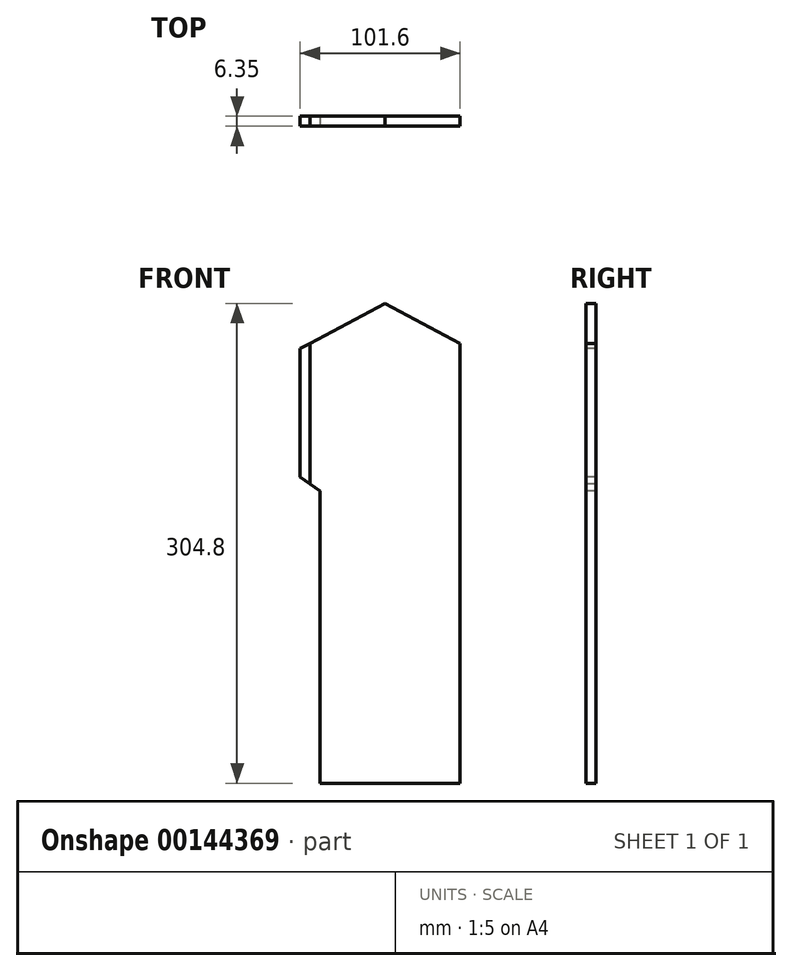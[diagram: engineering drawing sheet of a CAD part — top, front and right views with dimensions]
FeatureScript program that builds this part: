
annotation { "Feature Type Name" : "Feature", "Feature Type Description" : "" }
export const myFeature = defineFeature(function(context is Context, id is Id, definition is map)
    precondition{}
    {
        {
            var Q0;
            Q0=qCreatedBy(makeId("Front.planeOp"),FACE);
            var sketch = newSketch(context, id + "F0", { "sketchPlane" : qUnion([Q0])});
            skLineSegment(sketch, "E0.bottom", {"start": v(0, 0) * mm, "end": v(95.25, 0) * mm});
            skLineSegment(sketch, "E0.top", {"start": v(0, 279.4) * mm, "end": v(95.25, 279.4) * mm});
            skLineSegment(sketch, "E0.left", {"start": v(0, 0) * mm, "end": v(0, 279.4) * mm});
            skLineSegment(sketch, "E0.right", {"start": v(95.25, 0) * mm, "end": v(95.25, 279.4) * mm});
            skLineSegment(sketch, "E1", {"start": v(0, 279.4) * mm, "end": v(47.62, 304.8) * mm});
            skLineSegment(sketch, "E2", {"start": v(47.62, 304.8) * mm, "end": v(95.25, 279.4) * mm});
            skLineSegment(sketch, "E3", {"start": v(47.62, 304.8) * mm, "end": v(47.62, 279.4) * mm, "construction": true});
            skSolve(sketch);
        }
        {
            var Q0;
            Q0 = qSketchRegion(id + "F0", true);
            extrude(context, id + "F1", {"entities" : qUnion([Q0]), "depth" : 6.35 * mm});
        }
        {
            var Q0;
            Q0=makeQuery(id+"F1.opExtrude","CAP_FACE",FACE,{"disambiguationData":[OSD([sQuery(id+"F0.wireOp",EDGE,"E0.bottom"),sQuery(id+"F0.wireOp",EDGE,"E0.top"),sQuery(id+"F0.wireOp",EDGE,"E0.left"),sQuery(id+"F0.wireOp",EDGE,"E0.right")])],"isStart":false});
            var sketch = newSketch(context, id + "F2", { "sketchPlane" : qUnion([Q0])});
            skLineSegment(sketch, "E4", {"start": v(6.35, 0) * mm, "end": v(6.35, 177.8) * mm});
            skLineSegment(sketch, "E5", {"start": v(6.35, 177.8) * mm, "end": v(0, 182.28) * mm});
            skLineSegment(sketch, "E6", {"start": v(6.35, 0) * mm, "end": v(0, 0) * mm});
            skLineSegment(sketch, "E7", {"start": v(0, 0) * mm, "end": v(0, 182.28) * mm});
            skSolve(sketch);
        }
        {
            var Q0;
            Q0 = qSketchRegion(id + "F2", true);
            extrude(context, id + "F3", {"entities" : qUnion([Q0]), "operationType" : NewBodyOperationType.REMOVE, "oppositeDirection" : true, "depth" : 25.4 * mm});
        }
        {
            var Q0;
            Q0=makeQuery(id+"F1.opExtrude","CAP_FACE",FACE,{"disambiguationData":[OSD([sQuery(id+"F0.wireOp",EDGE,"E0.bottom"),sQuery(id+"F0.wireOp",EDGE,"E0.top"),sQuery(id+"F0.wireOp",EDGE,"E0.left"),sQuery(id+"F0.wireOp",EDGE,"E0.right")])],"isStart":false});
            var sketch = newSketch(context, id + "F4", { "sketchPlane" : qUnion([Q0])});
            skLineSegment(sketch, "E8", {"start": v(6.35, 177.8) * mm, "end": v(6.35, 185.57) * mm});
            skLineSegment(sketch, "E9", {"start": v(6.35, 185.57) * mm, "end": v(0, 190.06) * mm});
            skLineSegment(sketch, "E10", {"start": v(0, 190.06) * mm, "end": v(0, 182.28) * mm});
            skLineSegment(sketch, "E11", {"start": v(0, 182.28) * mm, "end": v(6.35, 177.8) * mm});
            skSolve(sketch);
        }
        {
            var Q0;
            Q0 = qSketchRegion(id + "F4", true);
            extrude(context, id + "F5", {"entities" : qUnion([Q0]), "operationType" : NewBodyOperationType.REMOVE, "oppositeDirection" : true, "depth" : 6.35 * mm});
        }
        {
            var Q0;
            Q0=makeQuery(id+"F1.opExtrude","CAP_FACE",FACE,{"disambiguationData":[OSD([sQuery(id+"F0.wireOp",EDGE,"E0.bottom"),sQuery(id+"F0.wireOp",EDGE,"E0.left"),sQuery(id+"F0.wireOp",EDGE,"E0.right"),sQuery(id+"F0.wireOp",EDGE,"E1"),sQuery(id+"F0.wireOp",EDGE,"E2")])],"isStart":false});
            var sketch = newSketch(context, id + "F6", { "sketchPlane" : qUnion([Q0])});
            skLineSegment(sketch, "E12", {"start": v(0, 279.4) * mm, "end": v(-6.35, 276.01) * mm});
            skLineSegment(sketch, "E13", {"start": v(-6.35, 276.01) * mm, "end": v(-6.35, 194.54) * mm});
            skLineSegment(sketch, "E14", {"start": v(-6.35, 194.54) * mm, "end": v(0, 190.06) * mm});
            skSolve(sketch);
        }
        {
            var Q0;
            Q0 = qSketchRegion(id + "F6", true);
            var Q1;
            Q1=makeQuery(id+"F6.imprint","IMPRINT",FACE,{"disambiguationData":[TD([[makeQuery(id+"F6.imprint","IMPRINT",EDGE,{"derivedFrom":sQuery(id+"F6.wireOp",EDGE,"E12")}),1.0]])]});
            extrude(context, id + "F7", {"entities" : qUnion([Q0, Q1]), "oppositeDirection" : true, "depth" : 6.35 * mm});
        }
    });
